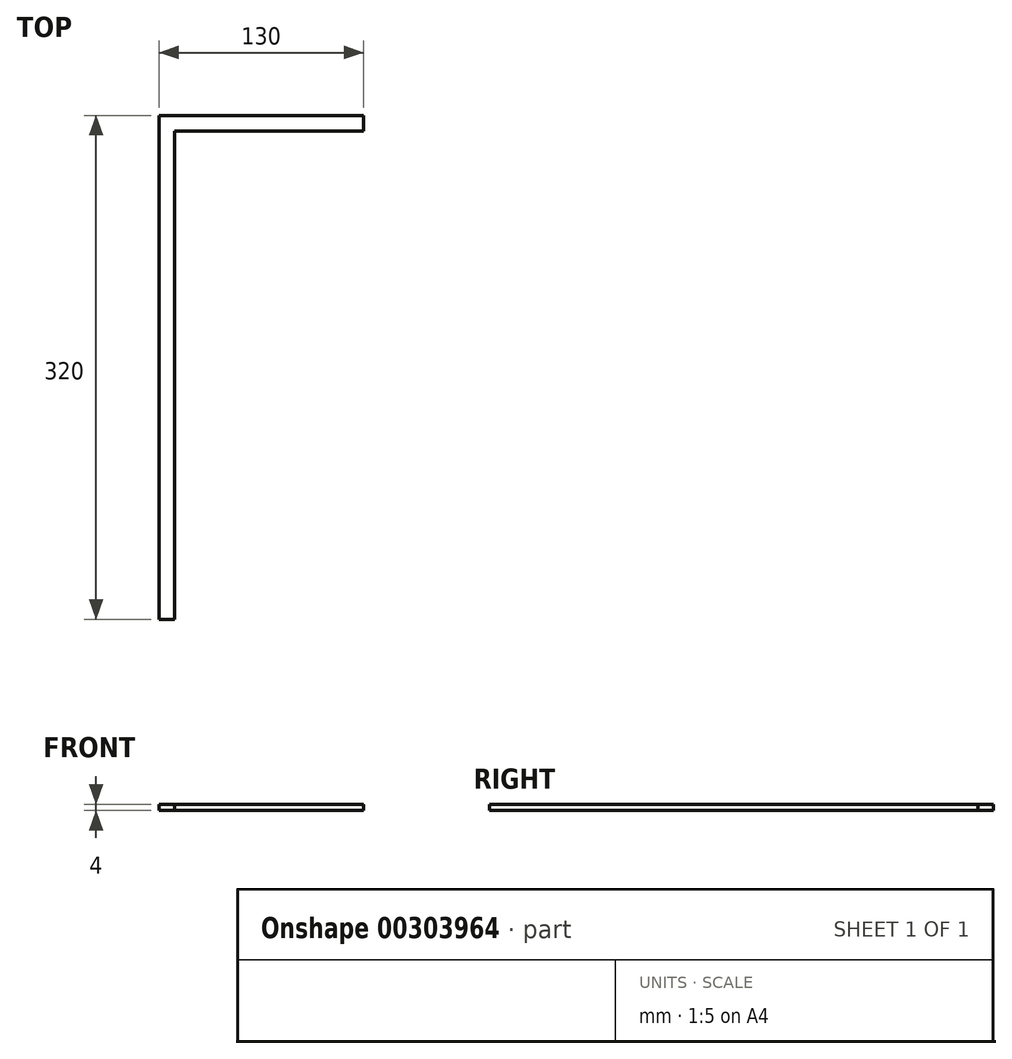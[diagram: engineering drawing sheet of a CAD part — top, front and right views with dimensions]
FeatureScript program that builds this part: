
annotation { "Feature Type Name" : "Feature", "Feature Type Description" : "" }
export const myFeature = defineFeature(function(context is Context, id is Id, definition is map)
    precondition{}
    {
        {
            var Q0;
            Q0=qCreatedBy(makeId("Top.planeOp"),FACE);
            var sketch = newSketch(context, id + "F0", { "sketchPlane" : qUnion([Q0])});
            skLineSegment(sketch, "E0", {"start": v(-10, 0) * mm, "end": v(-10, 320) * mm});
            skLineSegment(sketch, "E1", {"start": v(0, 310) * mm, "end": v(0, 0) * mm});
            skLineSegment(sketch, "E2", {"start": v(0, 0) * mm, "end": v(-10, 0) * mm});
            skLineSegment(sketch, "E3.bottom", {"start": v(-10, 320) * mm, "end": v(120, 320) * mm});
            skLineSegment(sketch, "E3.top", {"start": v(0, 310) * mm, "end": v(120, 310) * mm});
            skLineSegment(sketch, "E3.left", {"start": v(-10, 320) * mm, "end": v(-10, 310) * mm});
            skLineSegment(sketch, "E3.right", {"start": v(120, 320) * mm, "end": v(120, 310) * mm});
            skSolve(sketch);
        }
        {
            var Q0;
            Q0 = qSketchRegion(id + "F0", true);
            extrude(context, id + "F1", {"entities" : qUnion([Q0]), "depth" : 4 * mm});
        }
    });
